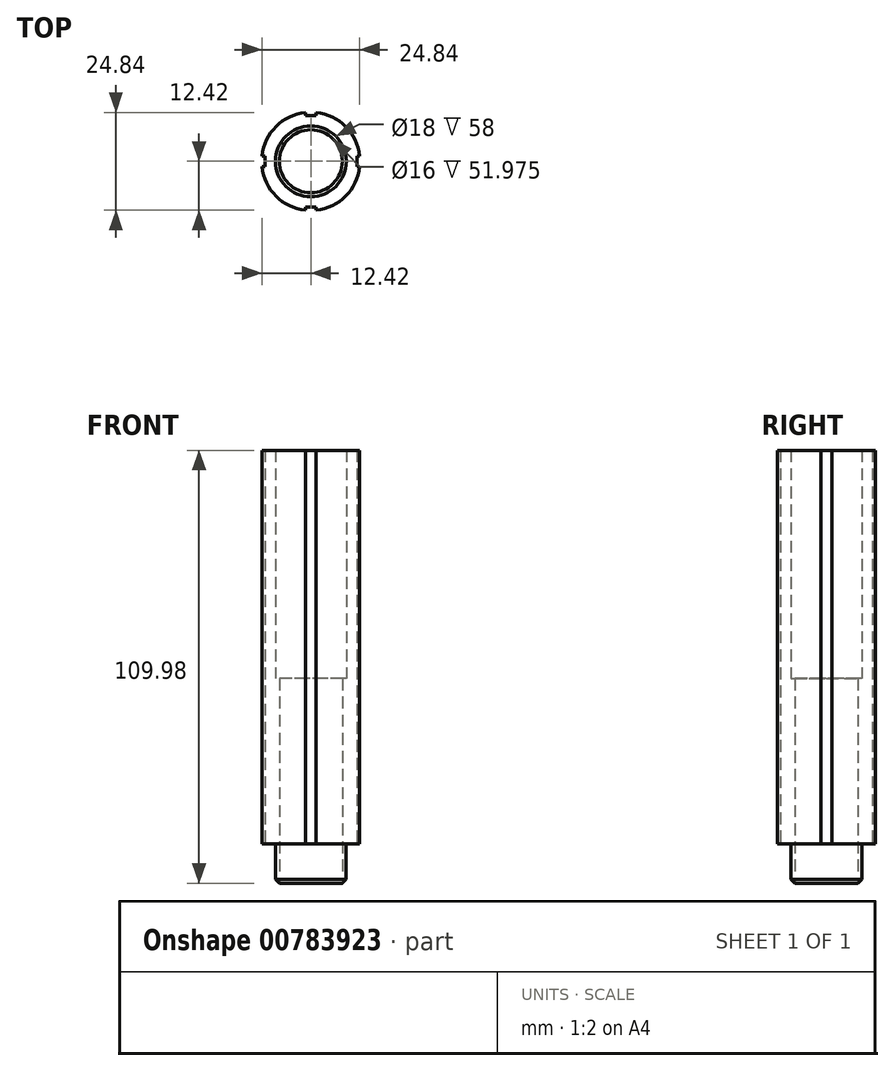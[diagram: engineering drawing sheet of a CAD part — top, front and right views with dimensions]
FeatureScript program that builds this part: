
annotation { "Feature Type Name" : "Feature", "Feature Type Description" : "" }
export const myFeature = defineFeature(function(context is Context, id is Id, definition is map)
    precondition{}
    {
        {
            var Q0;
            Q0=qCreatedBy(makeId("Top.planeOp"),FACE);
            var sketch = newSketch(context, id + "F0", { "sketchPlane" : qUnion([Q0])});
            skCircle(sketch, "E0", {"center": v(0, 0) * mm, "radius": 12.5 * mm});
            skPoint(sketch, "E1", {"position": v(-1.37, -12.42) * mm});
            skPoint(sketch, "E2", {"position": v(1.37, -12.42) * mm});
            skPoint(sketch, "E3", {"position": v(12.42, -1.37) * mm});
            skPoint(sketch, "E4", {"position": v(-12.42, -1.37) * mm});
            skPoint(sketch, "E5", {"position": v(-12.42, 1.37) * mm});
            skPoint(sketch, "E6", {"position": v(-1.37, 12.42) * mm});
            skPoint(sketch, "E7", {"position": v(1.37, 12.42) * mm});
            skPoint(sketch, "E8", {"position": v(12.42, 1.37) * mm});
            skLineSegment(sketch, "E9", {"start": v(-12.42, 1.37) * mm, "end": v(-11.67, 1.37) * mm});
            skLineSegment(sketch, "E10", {"start": v(-11.67, 1.37) * mm, "end": v(-11.67, -1.37) * mm});
            skLineSegment(sketch, "E11", {"start": v(-11.67, -1.38) * mm, "end": v(-12.42, -1.38) * mm});
            skLineSegment(sketch, "E12", {"start": v(12.42, 1.38) * mm, "end": v(11.67, 1.38) * mm});
            skLineSegment(sketch, "E13", {"start": v(11.67, 1.38) * mm, "end": v(11.67, -1.38) * mm});
            skLineSegment(sketch, "E14", {"start": v(11.67, -1.37) * mm, "end": v(12.42, -1.37) * mm});
            skLineSegment(sketch, "E15", {"start": v(-1.37, -12.42) * mm, "end": v(-1.37, -11.67) * mm});
            skLineSegment(sketch, "E16", {"start": v(-1.38, -11.67) * mm, "end": v(1.38, -11.67) * mm});
            skLineSegment(sketch, "E17", {"start": v(1.38, -11.67) * mm, "end": v(1.38, -12.42) * mm});
            skLineSegment(sketch, "E18", {"start": v(1.37, 12.42) * mm, "end": v(1.37, 11.67) * mm});
            skLineSegment(sketch, "E19", {"start": v(1.37, 11.67) * mm, "end": v(-1.37, 11.67) * mm});
            skLineSegment(sketch, "E20", {"start": v(-1.38, 11.67) * mm, "end": v(-1.38, 12.42) * mm});
            skPoint(sketch, "E21", {"position": v(11.67, 0) * mm});
            skCircle(sketch, "E22", {"center": v(0, 0) * mm, "radius": 9 * mm});
            skCircle(sketch, "E23", {"center": v(0, 0) * mm, "radius": 8 * mm});
            skSolve(sketch);
        }
        {
            var Q0;
            {var subQ1=sQuery(id+"F0.wireOp",EDGE,"E9");Q0=makeQuery(id+"F0.imprint","IMPRINT",FACE,{"disambiguationData":[TD([[makeQuery(id+"F0.imprint","IMPRINT",EDGE,{"derivedFrom":subQ1}),1.0]])]});}
            extrude(context, id + "F1", {"entities" : qUnion([Q0]), "depth" : 100 * mm, "offsetDistance" : 25.4 * mm});
        }
        {
            var Q0;
            Q0=qCreatedBy(makeId("Top.planeOp"),FACE);
            var sketch = newSketch(context, id + "F2", { "sketchPlane" : qUnion([Q0])});
            skCircle(sketch, "E24", {"center": v(0, 0) * mm, "radius": 9 * mm});
            skCircle(sketch, "E25", {"center": v(0, 0) * mm, "radius": 8 * mm});
            skSolve(sketch);
        }
        {
            var Q0;
            Q0=makeQuery(id+"F2.imprint","IMPRINT",FACE,{"disambiguationData":[TD([[makeQuery(id+"F2.imprint","IMPRINT",EDGE,{"derivedFrom":sQuery(id+"F2.wireOp",EDGE,"E24")}),1.0]])]});
            extrude(context, id + "F3", {"entities" : qUnion([Q0]), "operationType" : NewBodyOperationType.ADD, "depth" : 42 * mm, "offsetDistance" : 25.4 * mm});
        }
        {
            var Q0;
            Q0=qCreatedBy(makeId("Top.planeOp"),FACE);
            var sketch = newSketch(context, id + "F4", { "sketchPlane" : qUnion([Q0])});
            skCircle(sketch, "E26", {"center": v(0, 0) * mm, "radius": 8.97 * mm});
            skSolve(sketch);
        }
        {
            var Q0;
            Q0=makeQuery(id+"F4.imprint","IMPRINT",FACE,{"disambiguationData":[TD([[makeQuery(id+"F4.imprint","IMPRINT",EDGE,{"derivedFrom":sQuery(id+"F4.wireOp",EDGE,"E26")}),1.0]])]});
            extrude(context, id + "F5", {"entities" : qUnion([Q0]), "operationType" : NewBodyOperationType.ADD, "oppositeDirection" : true, "depth" : 10 * mm, "offsetDistance" : 25.4 * mm});
        }
        {
            var Q0;
            Q0=makeQuery(id+"F5.opExtrude","CAP_FACE",FACE,{"disambiguationData":[OSD([sQuery(id+"F4.wireOp",EDGE,"E26")])],"isStart":false});
            var sketch = newSketch(context, id + "F6", { "sketchPlane" : qUnion([Q0])});
            skCircle(sketch, "E27", {"center": v(0, 0) * mm, "radius": 8 * mm});
            skSolve(sketch);
        }
        {
            var Q0;
            Q0=sQuery(id+"F6.wireOp",VERTEX,"E27.center");
            var Q1;
            Q1=makeQuery(id+"F1.opExtrude","SWEPT_BODY",BODY,{"disambiguationData":[OSD([sQuery(id+"F0.wireOp",EDGE,"E0"),sQuery(id+"F0.wireOp",EDGE,"E9"),sQuery(id+"F0.wireOp",EDGE,"E10"),sQuery(id+"F0.wireOp",EDGE,"E11"),sQuery(id+"F0.wireOp",EDGE,"E12"),sQuery(id+"F0.wireOp",EDGE,"E13"),sQuery(id+"F0.wireOp",EDGE,"E14"),sQuery(id+"F0.wireOp",EDGE,"E15"),sQuery(id+"F0.wireOp",EDGE,"E16"),sQuery(id+"F0.wireOp",EDGE,"E17"),sQuery(id+"F0.wireOp",EDGE,"E18"),sQuery(id+"F0.wireOp",EDGE,"E19"),sQuery(id+"F0.wireOp",EDGE,"E20"),sQuery(id+"F0.wireOp",EDGE,"E22")])]});
            hole(context, id + "F7", {"style" : HoleStyle.SIMPLE, "endStyle" : HoleEndStyle.THROUGH, "holeDiameter" : 16 * mm, "majorDiameter" : 6.35 * mm, "isTappedThrough" : true, "tappedDepth" : 12.7 * mm, "tapClearance" : 3, "locations" : qUnion([Q0]), "scope" : qUnion([Q1])});
        }
        {
            var Q0;
            Q0=makeQuery(id+"F5.opExtrude","CAP_EDGE",EDGE,{"disambiguationData":[OSD([sQuery(id+"F4.wireOp",EDGE,"E26")])],"isStart":false});
            chamfer(context, id + "F8", {"entities" : qUnion([Q0]), "width" : 1 * mm, "tangentPropagation" : true});
        }
    });
